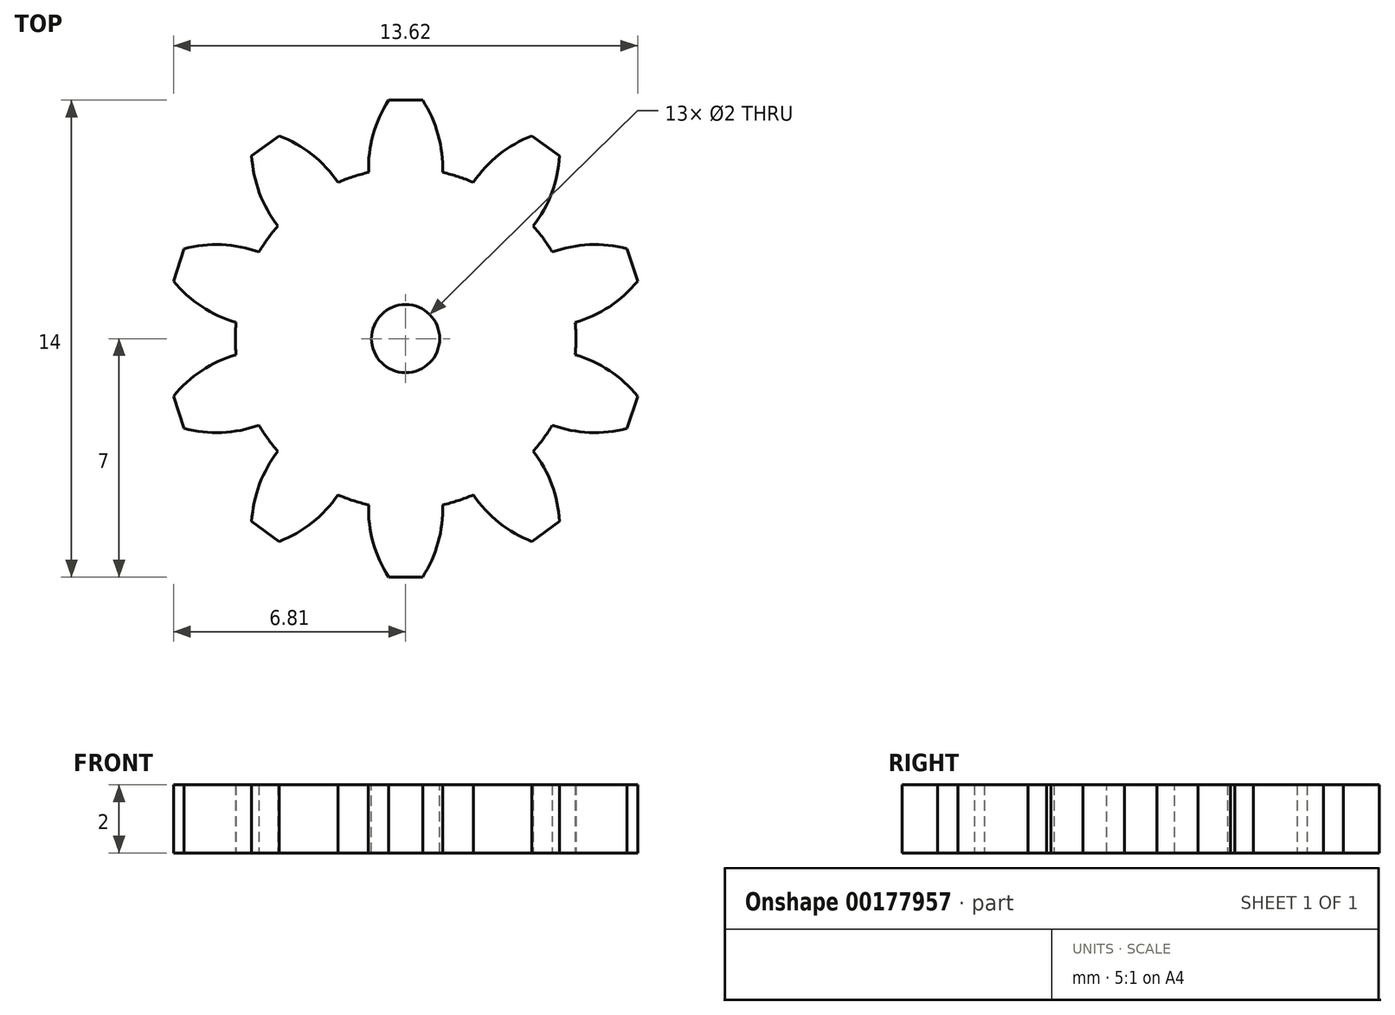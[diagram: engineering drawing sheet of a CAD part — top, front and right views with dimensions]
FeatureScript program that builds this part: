
annotation { "Feature Type Name" : "Feature", "Feature Type Description" : "" }
export const myFeature = defineFeature(function(context is Context, id is Id, definition is map)
    precondition{}
    {
        {
            var Q0;
            Q0=qCreatedBy(makeId("Top.planeOp"),FACE);
            var sketch = newSketch(context, id + "F0", { "sketchPlane" : qUnion([Q0])});
            skCircle(sketch, "E0", {"center": v(0, 0) * mm, "radius": 5 * mm});
            skLineSegment(sketch, "E1", {"start": v(0, 0) * mm, "end": v(0, 5) * mm, "construction": true});
            skLineSegment(sketch, "E2", {"start": v(0, 5) * mm, "end": v(0, 7) * mm});
            skLineSegment(sketch, "E3", {"start": v(0, 7) * mm, "end": v(-0.5, 7) * mm});
            skArc(sketch, "E4", {"start": v(-0.5, 7) * mm, "mid": v(-0.96, 5.98) * mm, "end": v(-1.09, 4.88) * mm});
            skLineSegment(sketch, "E5.MirrorCS", {"start": v(0, 7) * mm, "end": v(0.5, 7) * mm});
            skArc(sketch, "E6.MirrorCS", {"start": v(0.5, 7) * mm, "mid": v(0.96, 5.98) * mm, "end": v(1.09, 4.88) * mm});
            skArc(sketch, "E7.1.0", {"start": v(-4.52, 5.37) * mm, "mid": v(-4.3, 4.28) * mm, "end": v(-3.75, 3.3) * mm});
            skLineSegment(sketch, "E7.1.1", {"start": v(-4.11, 5.66) * mm, "end": v(-4.52, 5.37) * mm});
            skLineSegment(sketch, "E7.1.2", {"start": v(-4.11, 5.66) * mm, "end": v(-3.7, 5.96) * mm});
            skArc(sketch, "E7.1.3", {"start": v(-3.7, 5.96) * mm, "mid": v(-2.75, 5.4) * mm, "end": v(-1.99, 4.59) * mm});
            skArc(sketch, "E7.2.0", {"start": v(-6.81, 1.69) * mm, "mid": v(-5.99, 0.94) * mm, "end": v(-4.98, 0.47) * mm});
            skLineSegment(sketch, "E7.2.1", {"start": v(-6.66, 2.16) * mm, "end": v(-6.81, 1.69) * mm});
            skLineSegment(sketch, "E7.2.2", {"start": v(-6.66, 2.16) * mm, "end": v(-6.5, 2.64) * mm});
            skArc(sketch, "E7.2.3", {"start": v(-6.5, 2.64) * mm, "mid": v(-5.4, 2.76) * mm, "end": v(-4.3, 2.54) * mm});
            skArc(sketch, "E7.3.0", {"start": v(-6.5, -2.64) * mm, "mid": v(-5.4, -2.76) * mm, "end": v(-4.3, -2.54) * mm});
            skLineSegment(sketch, "E7.3.1", {"start": v(-6.66, -2.16) * mm, "end": v(-6.5, -2.64) * mm});
            skLineSegment(sketch, "E7.3.2", {"start": v(-6.66, -2.16) * mm, "end": v(-6.81, -1.69) * mm});
            skArc(sketch, "E7.3.3", {"start": v(-6.81, -1.69) * mm, "mid": v(-5.99, -0.94) * mm, "end": v(-4.98, -0.47) * mm});
            skArc(sketch, "E7.4.0", {"start": v(-3.7, -5.96) * mm, "mid": v(-2.75, -5.4) * mm, "end": v(-1.99, -4.59) * mm});
            skLineSegment(sketch, "E7.4.1", {"start": v(-4.11, -5.66) * mm, "end": v(-3.7, -5.96) * mm});
            skLineSegment(sketch, "E7.4.2", {"start": v(-4.11, -5.66) * mm, "end": v(-4.52, -5.37) * mm});
            skArc(sketch, "E7.4.3", {"start": v(-4.52, -5.37) * mm, "mid": v(-4.3, -4.28) * mm, "end": v(-3.75, -3.3) * mm});
            skArc(sketch, "E7.5.0", {"start": v(0.5, -7) * mm, "mid": v(0.96, -5.98) * mm, "end": v(1.09, -4.88) * mm});
            skLineSegment(sketch, "E7.5.1", {"start": v(0, -7) * mm, "end": v(0.5, -7) * mm});
            skLineSegment(sketch, "E7.5.2", {"start": v(0, -7) * mm, "end": v(-0.5, -7) * mm});
            skArc(sketch, "E7.5.3", {"start": v(-0.5, -7) * mm, "mid": v(-0.96, -5.98) * mm, "end": v(-1.09, -4.88) * mm});
            skArc(sketch, "E7.6.0", {"start": v(4.52, -5.37) * mm, "mid": v(4.3, -4.28) * mm, "end": v(3.75, -3.3) * mm});
            skLineSegment(sketch, "E7.6.1", {"start": v(4.11, -5.66) * mm, "end": v(4.52, -5.37) * mm});
            skLineSegment(sketch, "E7.6.2", {"start": v(4.11, -5.66) * mm, "end": v(3.7, -5.96) * mm});
            skArc(sketch, "E7.6.3", {"start": v(3.7, -5.96) * mm, "mid": v(2.75, -5.4) * mm, "end": v(1.99, -4.59) * mm});
            skArc(sketch, "E7.7.0", {"start": v(6.81, -1.69) * mm, "mid": v(5.99, -0.94) * mm, "end": v(4.98, -0.47) * mm});
            skLineSegment(sketch, "E7.7.1", {"start": v(6.66, -2.16) * mm, "end": v(6.81, -1.69) * mm});
            skLineSegment(sketch, "E7.7.2", {"start": v(6.66, -2.16) * mm, "end": v(6.5, -2.64) * mm});
            skArc(sketch, "E7.7.3", {"start": v(6.5, -2.64) * mm, "mid": v(5.4, -2.76) * mm, "end": v(4.3, -2.54) * mm});
            skArc(sketch, "E7.8.0", {"start": v(6.5, 2.64) * mm, "mid": v(5.4, 2.76) * mm, "end": v(4.3, 2.54) * mm});
            skLineSegment(sketch, "E7.8.1", {"start": v(6.66, 2.16) * mm, "end": v(6.5, 2.64) * mm});
            skLineSegment(sketch, "E7.8.2", {"start": v(6.66, 2.16) * mm, "end": v(6.81, 1.69) * mm});
            skArc(sketch, "E7.8.3", {"start": v(6.81, 1.69) * mm, "mid": v(5.99, 0.94) * mm, "end": v(4.98, 0.47) * mm});
            skArc(sketch, "E7.9.0", {"start": v(3.7, 5.96) * mm, "mid": v(2.75, 5.4) * mm, "end": v(1.99, 4.59) * mm});
            skLineSegment(sketch, "E7.9.1", {"start": v(4.11, 5.66) * mm, "end": v(3.7, 5.96) * mm});
            skLineSegment(sketch, "E7.9.2", {"start": v(4.11, 5.66) * mm, "end": v(4.52, 5.37) * mm});
            skArc(sketch, "E7.9.3", {"start": v(4.52, 5.37) * mm, "mid": v(4.3, 4.28) * mm, "end": v(3.75, 3.3) * mm});
            skSolve(sketch);
        }
        {
            var Q0;
            Q0=qSketchRegion(id+"F0",true);
            extrude(context, id + "F1", {"entities" : qUnion([Q0]), "depth" : 2 * mm});
        }
        {
            var Q0;
            Q0=makeQuery(id+"F1.opExtrude","CAP_FACE",FACE,{"disambiguationData":[OSD([sQuery(id+"F0.wireOp",EDGE,"E0"),sQuery(id+"F0.wireOp",EDGE,"E3"),sQuery(id+"F0.wireOp",EDGE,"E4"),sQuery(id+"F0.wireOp",EDGE,"E5.MirrorCS"),sQuery(id+"F0.wireOp",EDGE,"E6.MirrorCS"),sQuery(id+"F0.wireOp",EDGE,"E7.1.0"),sQuery(id+"F0.wireOp",EDGE,"E7.1.1"),sQuery(id+"F0.wireOp",EDGE,"E7.1.2"),sQuery(id+"F0.wireOp",EDGE,"E7.1.3"),sQuery(id+"F0.wireOp",EDGE,"E7.2.0"),sQuery(id+"F0.wireOp",EDGE,"E7.2.1"),sQuery(id+"F0.wireOp",EDGE,"E7.2.2"),sQuery(id+"F0.wireOp",EDGE,"E7.2.3"),sQuery(id+"F0.wireOp",EDGE,"E7.3.0"),sQuery(id+"F0.wireOp",EDGE,"E7.3.1"),sQuery(id+"F0.wireOp",EDGE,"E7.3.2"),sQuery(id+"F0.wireOp",EDGE,"E7.3.3"),sQuery(id+"F0.wireOp",EDGE,"E7.4.0"),sQuery(id+"F0.wireOp",EDGE,"E7.4.1"),sQuery(id+"F0.wireOp",EDGE,"E7.4.2"),sQuery(id+"F0.wireOp",EDGE,"E7.4.3"),sQuery(id+"F0.wireOp",EDGE,"E7.5.0"),sQuery(id+"F0.wireOp",EDGE,"E7.5.1"),sQuery(id+"F0.wireOp",EDGE,"E7.5.2"),sQuery(id+"F0.wireOp",EDGE,"E7.5.3"),sQuery(id+"F0.wireOp",EDGE,"E7.6.0"),sQuery(id+"F0.wireOp",EDGE,"E7.6.1"),sQuery(id+"F0.wireOp",EDGE,"E7.6.2"),sQuery(id+"F0.wireOp",EDGE,"E7.6.3"),sQuery(id+"F0.wireOp",EDGE,"E7.7.0"),sQuery(id+"F0.wireOp",EDGE,"E7.7.1"),sQuery(id+"F0.wireOp",EDGE,"E7.7.2"),sQuery(id+"F0.wireOp",EDGE,"E7.7.3"),sQuery(id+"F0.wireOp",EDGE,"E7.8.0"),sQuery(id+"F0.wireOp",EDGE,"E7.8.1"),sQuery(id+"F0.wireOp",EDGE,"E7.8.2"),sQuery(id+"F0.wireOp",EDGE,"E7.8.3"),sQuery(id+"F0.wireOp",EDGE,"E7.9.0"),sQuery(id+"F0.wireOp",EDGE,"E7.9.1"),sQuery(id+"F0.wireOp",EDGE,"E7.9.2"),sQuery(id+"F0.wireOp",EDGE,"E7.9.3"),sQuery(id+"F0.wireOp",EDGE,"E7.10.0"),sQuery(id+"F0.wireOp",EDGE,"E7.10.1"),sQuery(id+"F0.wireOp",EDGE,"E7.10.2"),sQuery(id+"F0.wireOp",EDGE,"E7.10.3"),sQuery(id+"F0.wireOp",EDGE,"E7.11.0"),sQuery(id+"F0.wireOp",EDGE,"E7.11.1"),sQuery(id+"F0.wireOp",EDGE,"E7.11.2"),sQuery(id+"F0.wireOp",EDGE,"E7.11.3"),sQuery(id+"F0.wireOp",EDGE,"E7.12.0"),sQuery(id+"F0.wireOp",EDGE,"E7.12.1"),sQuery(id+"F0.wireOp",EDGE,"E7.12.2"),sQuery(id+"F0.wireOp",EDGE,"E7.12.3"),sQuery(id+"F0.wireOp",EDGE,"E7.13.0"),sQuery(id+"F0.wireOp",EDGE,"E7.13.1"),sQuery(id+"F0.wireOp",EDGE,"E7.13.2"),sQuery(id+"F0.wireOp",EDGE,"E7.13.3"),sQuery(id+"F0.wireOp",EDGE,"E7.14.0"),sQuery(id+"F0.wireOp",EDGE,"E7.14.1"),sQuery(id+"F0.wireOp",EDGE,"E7.14.2"),sQuery(id+"F0.wireOp",EDGE,"E7.14.3"),sQuery(id+"F0.wireOp",EDGE,"E7.15.0"),sQuery(id+"F0.wireOp",EDGE,"E7.15.1"),sQuery(id+"F0.wireOp",EDGE,"E7.15.2"),sQuery(id+"F0.wireOp",EDGE,"E7.15.3")])],"isStart":false});
            var sketch = newSketch(context, id + "F2", { "sketchPlane" : qUnion([Q0])});
            skCircle(sketch, "E8", {"center": v(0, 0) * mm, "radius": 1 * mm});
            skSolve(sketch);
        }
        {
            var Q0;
            Q0=qSketchRegion(id+"F2",true);
            extrude(context, id + "F3", {"entities" : qUnion([Q0]), "operationType" : NewBodyOperationType.REMOVE, "endBound" : BoundingType.THROUGH_ALL, "oppositeDirection" : true, "depth" : 25 * mm});
        }
    });
